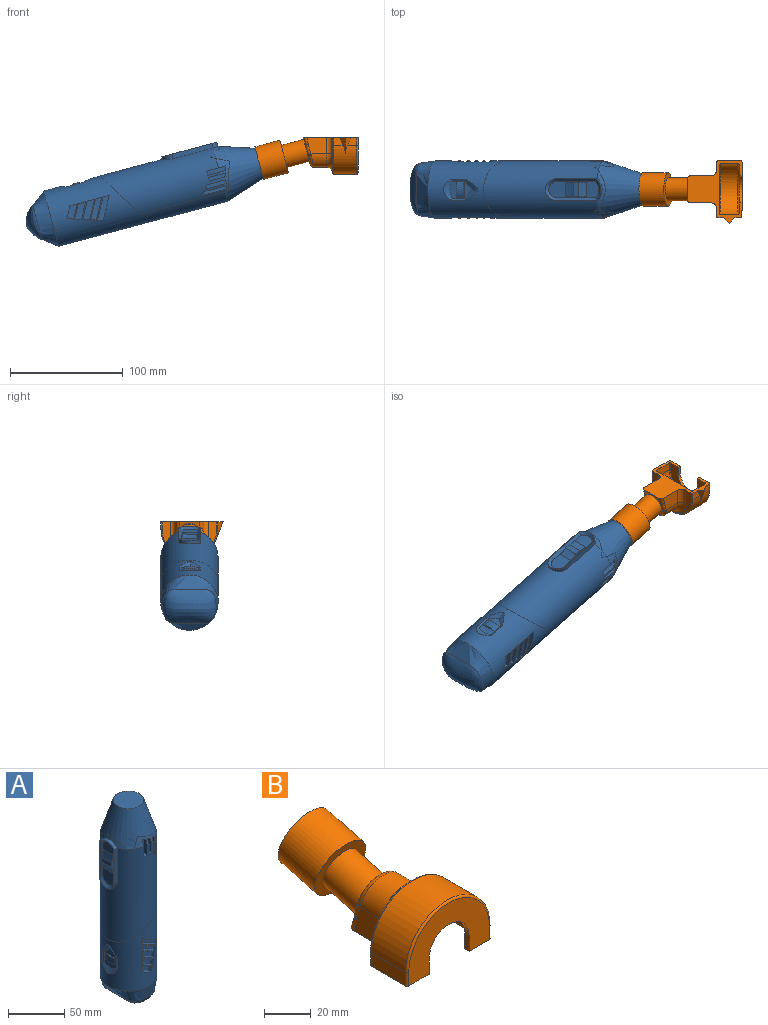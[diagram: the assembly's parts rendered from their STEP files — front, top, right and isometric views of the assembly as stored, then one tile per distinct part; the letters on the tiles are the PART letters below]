
ASSEMBLY  parts=2 mates=1
PART A: 121 faces, bbox 54.5x52.2x215.4 mm
  f0: cylinder r=9.53mm len=19.05mm, axis (-1,0,0), area 95.9mm2, adj f1,f2,f5,f20
  f1: plane 36.71x4.14mm, normal (0,1,0), area 152mm2, adj f0,f3,f7,f20
  f2: plane 37.21x4.55mm, normal (0,-1,0), area 152.3mm2, adj f0,f3,f5,f20
  f3: cylinder r=11.92mm len=19.05mm, axis (-1,0,0), area 88.1mm2, adj f1,f2,f6,f14,f20
  f4: plane 46.37x14.38mm, normal (-1,0,0), area 360.3mm2, adj f5,f6,f7,f9,f10,f11,f12
  f5: bspline ~46.59x19.05mm, area 212.8mm2, adj f0,f2,f4,f6,f7
  f6: bspline ~19.05x5.69mm, area 64.6mm2, adj f3,f4,f5,f7
  f7: plane 36.71x2.54mm, normal (-0.74,-0.67,0), area 123.9mm2, adj f1,f4,f5,f6
  f8: plane 12.7x4.89mm, normal (-1,0,0), area 62.1mm2, adj f9,f10,f11,f12
  f9: plane 19.47x1.9mm, normal (0,-1,0), area 22mm2, adj f4,f8,f11,f12
  f10: plane 19.47x1.9mm, normal (0,1,0), area 22mm2, adj f4,f8,f11,f12
  f11: cylinder r=64.91mm len=12.7mm, axis (0,-1,0), area 95.7mm2, adj f4,f8,f9,f10
  f12: cylinder r=64.91mm len=12.7mm, axis (0,-1,0), area 95.7mm2, adj f4,f8,f9,f10
  f13: cone r=13.66mm half-angle=18deg, axis (0,0,-1), area 4027.3mm2, adj f14,f15,f16,f17,f18,f21,f22
  f14: cone r=13.66mm half-angle=18deg, axis (0,0,-1), area 119mm2, adj f3,f13,f20
  f15: cone r=13.66mm half-angle=18deg, axis (0,0,-1), area 166.5mm2, adj f13,f20,f88,f89,f90,f93,f94,f95
  f16: cylinder r=25.4mm len=154.94mm, axis (0,0,1), area 12468.6mm2, adj f13,f20,f23,f24,f25,f26,f28,f29
  f17: cylinder r=25.4mm len=4.84mm, axis (0,0,1), area 14.8mm2, adj f13,f20
  f18: cylinder r=25.4mm len=4.84mm, axis (0,0,1), area 14.8mm2, adj f13,f20
  f19: plane 20.55x15.37mm, normal (-1,0,0), area 152.9mm2, adj f111,f112,f113,f114,f115,f116,f117,f118
  f20: cylinder r=25.4mm len=103.95mm, axis (0,0,1), area 9519.3mm2, adj f0,f1,f2,f3,f14,f15,f16,f17
  f21: cone r=13.66mm half-angle=18deg, axis (0,0,-1), area 166.5mm2, adj f13,f20,f44,f45,f46,f49,f50,f51
  f22: plane 27.32x27.32mm, normal (0,0,1), area 586.1mm2, adj f13
  f23: plane 10.43x5.57mm, normal (0.47,0,0.88), area 51mm2, adj f16,f24,f26,f27
  f24: plane 6.8x3.61mm, normal (1,0,0), area 24.6mm2, adj f16,f23,f25,f27
  f25: plane 12.28x6.55mm, normal (-0.47,0,-0.88), area 59.7mm2, adj f16,f24,f26,f27
  f26: plane 5.84x4.35mm, normal (-0.95,0,0.3), area 25.5mm2, adj f16,f23,f25,f27
  f27: plane 12.32x12.23mm, normal (0,-1,0), area 76.9mm2, adj f23,f24,f25,f26
  f28: plane 6.8x3.61mm, normal (1,0,0), area 24.6mm2, adj f16,f29,f31,f32
  f29: plane 14.37x7.67mm, normal (-0.47,0,-0.88), area 68.6mm2, adj f16,f28,f30,f32
  f30: plane 5.85x3.98mm, normal (-0.95,0,0.3), area 22.7mm2, adj f16,f29,f31,f32
  f31: plane 12.51x6.68mm, normal (0.47,0,0.88), area 60.8mm2, adj f16,f28,f30,f32
  f32: plane 14.32x13.44mm, normal (0,-1,0), area 91.1mm2, adj f28,f29,f30,f31
  f33: plane 5.86x3.4mm, normal (-0.95,0,0.3), area 18.5mm2, adj f16,f34,f36,f37
  f34: plane 14.72x7.86mm, normal (0.47,0,0.88), area 69.9mm2, adj f16,f33,f35,f37
  f35: plane 6.8x3.61mm, normal (1,0,0), area 24.6mm2, adj f16,f34,f36,f37
  f36: plane 16.64x8.91mm, normal (-0.47,0,-0.88), area 76.3mm2, adj f16,f33,f35,f37
  f37: plane 16.52x14.6mm, normal (0,-1,0), area 106mm2, adj f33,f34,f35,f36
  f38: plane 18.85x10.14mm, normal (0.47,0,0.88), area 81.6mm2, adj f16,f39,f41,f42
  f39: plane 5.79x3.61mm, normal (1,0,0), area 20.9mm2, adj f16,f38,f40,f42
  f40: plane 20.55x11.1mm, normal (-0.47,0,-0.88), area 83.9mm2, adj f16,f39,f41,f42
  f41: plane 5x1.77mm, normal (-0.95,0,0.3), area 6.7mm2, adj f16,f38,f40,f42
  f42: plane 20.18x15.69mm, normal (0,-1,0), area 112.3mm2, adj f38,f39,f40,f41
  f43: plane 4.53x3.99mm, normal (0,0,1), area 17.2mm2, adj f20,f44,f45,f47
  f44: plane 17.35x4mm, normal (1,0,0), area 61.6mm2, adj f20,f21,f43,f46,f47
  f45: plane 16.39x4.53mm, normal (-1,0,0), area 69mm2, adj f20,f21,f43,f46,f47
  f46: plane 4.01x2.7mm, normal (-0.23,0,-0.97), area 9.4mm2, adj f21,f44,f45,f47
  f47: plane 17.32x3.99mm, normal (0,-1,0), area 67.3mm2, adj f43,f44,f45,f46
  f48: plane 4.57x3.3mm, normal (0,0,1), area 14.7mm2, adj f20,f49,f50,f52
  f49: plane 15.16x4.29mm, normal (-1,0,0), area 61.7mm2, adj f20,f21,f48,f51,f52
  f50: plane 15.92x4.57mm, normal (1,0,0), area 68.3mm2, adj f20,f21,f48,f51,f52
  f51: plane 3.31x2.93mm, normal (-0.23,0,-0.97), area 9.8mm2, adj f21,f49,f50,f52
  f52: plane 15.92x3.3mm, normal (0,-1,0), area 51.3mm2, adj f48,f49,f50,f51
  f53: plane 3.76x3.29mm, normal (0.64,0,0.77), area 13.7mm2, adj f20,f54,f55,f57
  f54: plane 17.31x3.74mm, normal (1,0,0), area 62.2mm2, adj f20,f21,f53,f56,f57
  f55: plane 19.26x2.64mm, normal (-1,0,0), area 49.1mm2, adj f20,f21,f53,f56,f57
  f56: plane 3.27x2.47mm, normal (-0.23,0,-0.97), area 6.9mm2, adj f21,f54,f55,f57
  f57: plane 20.02x3.26mm, normal (0,-1,0), area 59.6mm2, adj f53,f54,f55,f56
  f58: plane 2.89x2.42mm, normal (0.64,0,0.77), area 3.3mm2, adj f20,f59,f60
  f59: plane 20.44x1.73mm, normal (1,0,0), area 33.9mm2, adj f20,f21,f58,f60,f61
  f60: plane 22.83x2.87mm, normal (0,-1,0), area 59.3mm2, adj f20,f21,f58,f59,f61
  f61: plane 1.55x0.78mm, normal (-0.23,0,-0.97), area 0.6mm2, adj f21,f59,f60
  f62: plane 18.55x9.97mm, normal (-0.47,0,-0.88), area 81mm2, adj f16,f63,f65,f66
  f63: plane 4.99x2.63mm, normal (-0.95,0,0.3), area 11.6mm2, adj f16,f62,f64,f66
  f64: plane 16.89x9.05mm, normal (0.47,0,0.88), area 77mm2, adj f16,f63,f65,f66
  f65: plane 5.79x3.61mm, normal (1,0,0), area 20.9mm2, adj f16,f62,f64,f66
  f66: plane 18.33x14.7mm, normal (0,-1,0), area 101.5mm2, adj f62,f63,f64,f65
  f67: plane 10.43x5.57mm, normal (0.47,0,0.88), area 51mm2, adj f16,f68,f70,f71
  f68: plane 5.84x4.35mm, normal (-0.95,0,0.3), area 25.5mm2, adj f16,f67,f69,f71
  f69: plane 12.28x6.55mm, normal (-0.47,0,-0.88), area 59.7mm2, adj f16,f68,f70,f71
  f70: plane 6.8x3.61mm, normal (1,0,0), area 24.6mm2, adj f16,f67,f69,f71
  f71: plane 12.32x12.23mm, normal (0,1,0), area 76.9mm2, adj f67,f68,f69,f70
  f72: plane 6.8x3.61mm, normal (1,0,0), area 24.6mm2, adj f16,f73,f75,f76
  f73: plane 12.51x6.68mm, normal (0.47,0,0.88), area 60.8mm2, adj f16,f72,f74,f76
  f74: plane 5.85x3.98mm, normal (-0.95,0,0.3), area 22.7mm2, adj f16,f73,f75,f76
  f75: plane 14.37x7.67mm, normal (-0.47,0,-0.88), area 68.6mm2, adj f16,f72,f74,f76
  f76: plane 14.32x13.44mm, normal (0,1,0), area 91.1mm2, adj f72,f73,f74,f75
  f77: plane 5.86x3.4mm, normal (-0.95,0,0.3), area 18.5mm2, adj f16,f78,f80,f81
  f78: plane 16.64x8.91mm, normal (-0.47,0,-0.88), area 76.3mm2, adj f16,f77,f79,f81
  f79: plane 6.8x3.61mm, normal (1,0,0), area 24.6mm2, adj f16,f78,f80,f81
  f80: plane 14.72x7.86mm, normal (0.47,0,0.88), area 69.9mm2, adj f16,f77,f79,f81
  f81: plane 16.52x14.6mm, normal (0,1,0), area 106mm2, adj f77,f78,f79,f80
  f82: plane 18.85x10.14mm, normal (0.47,0,0.88), area 81.6mm2, adj f16,f83,f85,f86
  f83: plane 5x1.77mm, normal (-0.95,0,0.3), area 6.7mm2, adj f16,f82,f84,f86
  f84: plane 20.55x11.1mm, normal (-0.47,0,-0.88), area 83.9mm2, adj f16,f83,f85,f86
  f85: plane 5.79x3.61mm, normal (1,0,0), area 20.9mm2, adj f16,f82,f84,f86
  f86: plane 20.18x15.69mm, normal (0,1,0), area 112.3mm2, adj f82,f83,f84,f85
  f87: plane 4.53x3.99mm, normal (0,0,1), area 17.2mm2, adj f20,f88,f89,f91
  f88: plane 17.35x4mm, normal (1,0,0), area 61.6mm2, adj f15,f20,f87,f90,f91
  f89: plane 16.39x4.53mm, normal (-1,0,0), area 69mm2, adj f15,f20,f87,f90,f91
  f90: plane 4.01x2.7mm, normal (-0.23,0,-0.97), area 9.4mm2, adj f15,f88,f89,f91
  f91: plane 17.32x3.99mm, normal (0,1,0), area 67.3mm2, adj f87,f88,f89,f90
  f92: plane 4.57x3.3mm, normal (0,0,1), area 14.7mm2, adj f20,f93,f94,f96
  f93: plane 15.92x4.57mm, normal (1,0,0), area 68.3mm2, adj f15,f20,f92,f95,f96
  f94: plane 15.16x4.29mm, normal (-1,0,0), area 61.7mm2, adj f15,f20,f92,f95,f96
  f95: plane 3.31x2.93mm, normal (-0.23,0,-0.97), area 9.8mm2, adj f15,f93,f94,f96
  f96: plane 15.92x3.3mm, normal (0,1,0), area 51.3mm2, adj f92,f93,f94,f95
  f97: plane 3.76x3.29mm, normal (0.64,0,0.77), area 13.7mm2, adj f20,f98,f99,f101
  f98: plane 17.31x3.74mm, normal (1,0,0), area 62.2mm2, adj f15,f20,f97,f100,f101
  f99: plane 19.26x2.64mm, normal (-1,0,0), area 49.1mm2, adj f15,f20,f97,f100,f101
  f100: plane 3.27x2.47mm, normal (-0.23,0,-0.97), area 6.9mm2, adj f15,f98,f99,f101
  f101: plane 20.02x3.26mm, normal (0,1,0), area 59.6mm2, adj f97,f98,f99,f100
  f102: plane 2.89x2.42mm, normal (0.64,0,0.77), area 3.3mm2, adj f20,f103,f104
  f103: plane 20.44x1.73mm, normal (1,0,0), area 33.9mm2, adj f15,f20,f102,f104,f105
  f104: plane 22.83x2.87mm, normal (0,1,0), area 59.3mm2, adj f15,f20,f102,f103,f105
  f105: plane 1.55x0.78mm, normal (-0.23,0,-0.97), area 0.6mm2, adj f15,f103,f104
  f106: plane 18.55x9.97mm, normal (-0.47,0,-0.88), area 81mm2, adj f16,f107,f109,f110
  f107: plane 5.79x3.61mm, normal (1,0,0), area 20.9mm2, adj f16,f106,f108,f110
  f108: plane 16.89x9.05mm, normal (0.47,0,0.88), area 77mm2, adj f16,f107,f109,f110
  f109: plane 4.99x2.63mm, normal (-0.95,0,0.3), area 11.6mm2, adj f16,f106,f108,f110
  f110: plane 18.33x14.7mm, normal (0,1,0), area 101.5mm2, adj f106,f107,f108,f109
  f111: bspline ~13.45x12.24mm, area 54.8mm2, adj f16,f19,f112,f113
  f112: bspline ~13.6x1.73mm, area 23.7mm2, adj f16,f19,f111,f114
  f113: plane 12.81x10.4mm, normal (-0.9,0.28,-0.34), area 44.4mm2, adj f16,f19,f111,f115
  f114: bspline ~24.33x7.15mm, area 80.9mm2, adj f16,f19,f112,f115
  f115: bspline ~14.34x1.75mm, area 25.7mm2, adj f16,f19,f113,f114
  f116: plane 14.61x1.88mm, normal (0,0,1), area 18.6mm2, adj f19,f118
  f117: plane 14.61x1.88mm, normal (0,0,-1), area 18.6mm2, adj f19,f118
  f118: cylinder r=15.12mm len=14.61mm, axis (0,0,-1), area 104.5mm2, adj f19,f116,f117
  f119: bspline ~50.78x50.75mm, area 2027mm2, adj f16,f120
  f120: bspline ~47.14x31.52mm, area 1717.1mm2, adj f119
PART B: 49 faces, bbox 57.8x92x38.3 mm
  f0: plane 31.25x24.25mm, normal (0,1,0), area 162.4mm2, adj f4,f33,f34,f47,f48
  f1: plane 18x6.61mm, normal (0,0.97,0.26), area 54.7mm2, adj f4,f21,f39,f45
  f2: cylinder r=25.25mm len=50.5mm, axis (0,1,0), area 1620.2mm2, adj f3,f6,f11,f25,f26,f34,f37
  f3: plane 8.33x7mm, normal (1,0,0), area 47.7mm2, adj f2,f4,f26,f35
  f4: plane 55.54x48.94mm, normal (0,0,-1), area 949.7mm2, adj f0,f1,f3,f5,f6,f7,f9,f10
  f5: plane 15.3x7mm, normal (-1,0,0), area 107.1mm2, adj f4,f15,f29,f32
  f6: plane 8.33x7mm, normal (1,0,0), area 47.7mm2, adj f2,f4,f25,f38
  f7: plane 17.9x14.25mm, normal (-1,0,0), area 229.3mm2, adj f4,f8,f44,f45,f48
  f8: cylinder r=12mm len=24mm, axis (0,-1,0), area 473.8mm2, adj f7,f9,f41,f42,f43,f47
  f9: plane 17.9x14.25mm, normal (1,0,0), area 229.3mm2, adj f4,f8,f39,f40,f46
  f10: plane 43.2x28.6mm, normal (0,1,0), area 614.4mm2, adj f4,f17,f18,f19,f30,f31,f32
  f11: plane 20.6x7mm, normal (-1,0,0), area 144.2mm2, adj f2,f4,f33,f36
  f12: plane 48.5x31.25mm, normal (0,-1,0), area 842.3mm2, adj f4,f17,f18,f19,f36,f37,f38
  f13: plane 31.25x24.25mm, normal (0,1,0), area 162.4mm2, adj f4,f34,f35,f46,f47
  f14: plane 15.3x7mm, normal (1,0,0), area 107.1mm2, adj f4,f15,f27,f30
  f15: cylinder r=22.6mm len=45.2mm, axis (0,1,0), area 1086.3mm2, adj f5,f14,f28,f31
  f16: plane 43.2x28.6mm, normal (0,-1,0), area 1035.3mm2, adj f4,f27,f28,f29
  f17: plane 8x2.65mm, normal (-1,0,0), area 21.2mm2, adj f4,f10,f12,f19
  f18: plane 8x2.65mm, normal (1,0,0), area 21.2mm2, adj f4,f10,f12,f19
  f19: cylinder r=12.05mm len=24.1mm, axis (0,-1,0), area 100.3mm2, adj f10,f12,f17,f18
  f20: plane 17.84x7.79mm, normal (0,0.97,0.26), area 43.3mm2, adj f21,f42
  f21: cylinder r=10.25mm len=25.28mm, axis (0,-0.97,-0.26), area 1333.1mm2, adj f1,f20,f24,f40,f41,f43,f44
  f22: cylinder r=14.9mm len=34.67mm, axis (0,-0.97,-0.26), area 2134.5mm2, adj f23,f24
  f23: plane 29.8x28.79mm, normal (0,0.97,0.26), area 697.5mm2, adj f22
  f24: plane 29.8x28.79mm, normal (0,-0.97,-0.26), area 367.4mm2, adj f21,f22
  f25: plane 14.51x6.23mm, normal (0.7,-0.66,0.28), area 43mm2, adj f2,f4,f6,f26
  f26: plane 14.51x6.23mm, normal (0.7,0.66,0.28), area 43mm2, adj f2,f3,f4,f25
  f27: cylinder r=1mm len=7mm, axis (0,0,1), area 11mm2, adj f4,f14,f16,f28
  f28: torus R=21.6mm, axis (0,-1,0), area 109.7mm2, adj f15,f16,f27,f29
  f29: cylinder r=1mm len=7mm, axis (0,0,-1), area 11mm2, adj f4,f5,f16,f28
  f30: cylinder r=1mm len=7mm, axis (0,0,-1), area 11mm2, adj f4,f10,f14,f31
  f31: torus R=21.6mm, axis (0,-1,0), area 109.7mm2, adj f10,f15,f30,f32
  f32: cylinder r=1mm len=7mm, axis (0,0,1), area 11mm2, adj f4,f5,f10,f31
  f33: cylinder r=1mm len=7mm, axis (0,0,-1), area 11mm2, adj f0,f4,f11,f34
  f34: torus R=24.25mm, axis (0,-1,0), area 122.8mm2, adj f0,f2,f13,f33,f35
  f35: cylinder r=1mm len=7mm, axis (0,0,1), area 11mm2, adj f3,f4,f13,f34
  f36: cylinder r=1mm len=7mm, axis (0,0,1), area 11mm2, adj f4,f11,f12,f37
  f37: torus R=24.25mm, axis (0,-1,0), area 122.8mm2, adj f2,f12,f36,f38
  f38: cylinder r=1mm len=7mm, axis (0,0,-1), area 11mm2, adj f4,f6,f12,f37
  f39: cylinder r=3mm len=7.39mm, axis (0,-0.26,0.97), area 30.4mm2, adj f1,f4,f9,f40
  f40: bspline ~10.49x5.63mm, area 33.4mm2, adj f9,f21,f39,f41
  f41: bspline ~5.6x4.1mm, area 6.3mm2, adj f8,f21,f40,f42
  f42: bspline ~23.78x10.38mm, area 130.9mm2, adj f8,f20,f41,f43
  f43: bspline ~5.6x4.1mm, area 6.3mm2, adj f8,f21,f42,f44
  f44: bspline ~11.13x6.11mm, area 33.3mm2, adj f7,f21,f43,f45
  f45: cylinder r=3mm len=7.39mm, axis (0,0.26,-0.97), area 30.4mm2, adj f1,f4,f7,f44
  f46: cylinder r=5mm len=14.25mm, axis (0,0,1), area 111.9mm2, adj f4,f9,f13,f47
  f47: torus R=17mm, axis (0,-1,0), area 340.9mm2, adj f0,f8,f13,f46,f48
  f48: cylinder r=5mm len=14.25mm, axis (0,0,-1), area 111.9mm2, adj f0,f4,f7,f47
PLACE A rot(axis=(0,1,0),75.1deg) t=(-39.53,25.47,14.4)mm
PLACE B rot(axis=(-0.71,0.71,0),180deg) t=(25.47,25.47,36.96)mm fixed
MATE revolute A.f13 <-> B.f22  axis (0.97,0,0.26) through (-39.53,25.47,14.4)mm
